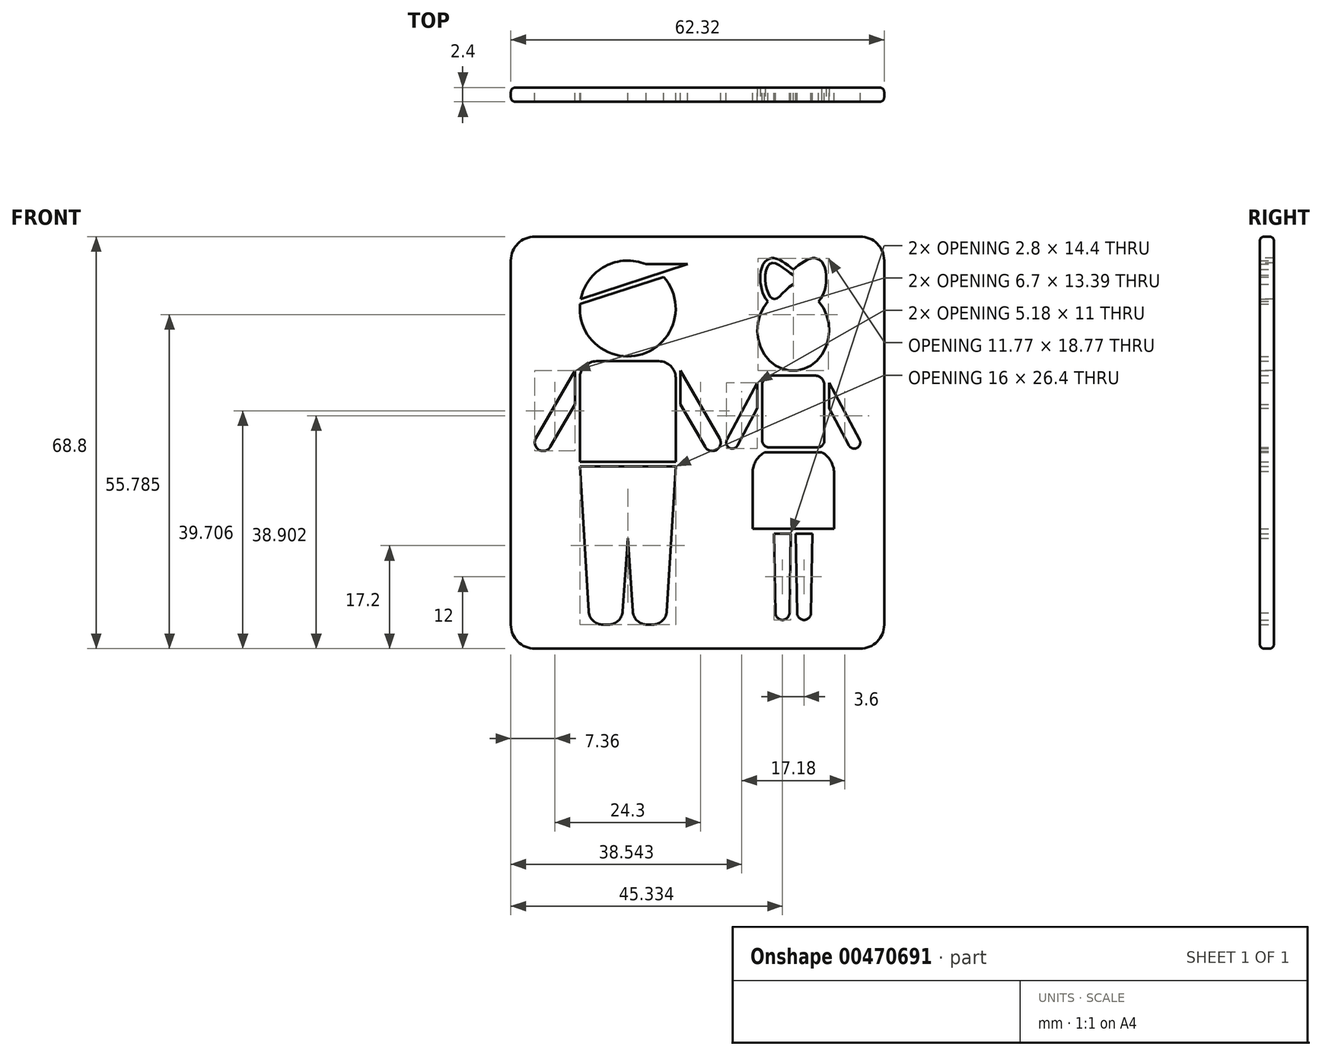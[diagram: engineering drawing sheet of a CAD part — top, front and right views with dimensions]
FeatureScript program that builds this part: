
annotation { "Feature Type Name" : "Feature", "Feature Type Description" : "" }
export const myFeature = defineFeature(function(context is Context, id is Id, definition is map)
    precondition{}
    {
        {
            var Q0;
            Q0=qCreatedBy(makeId("Front.planeOp"),FACE);
            var sketch = newSketch(context, id + "F0", { "sketchPlane" : qUnion([Q0])});
            skLineSegment(sketch, "E0", {"start": v(-25, 66) * mm, "end": v(-25, 0) * mm, "construction": true});
            skArc(sketch, "E1", {"start": v(-21.19, 75.25) * mm, "mid": v(-29.7, 74.83) * mm, "end": v(-34.8, 68) * mm});
            skLineSegment(sketch, "E2.bottom", {"start": v(-31.5, 55) * mm, "end": v(-18.5, 55) * mm});
            skLineSegment(sketch, "E2.top", {"start": v(-35, 34) * mm, "end": v(-15, 34) * mm});
            skLineSegment(sketch, "E2.left", {"start": v(-35, 51.5) * mm, "end": v(-35, 34) * mm});
            skLineSegment(sketch, "E2.right", {"start": v(-15, 51.5) * mm, "end": v(-15, 34) * mm});
            skPoint(sketch, "E2.middle", {"position": v(-25, 44.5) * mm});
            skPoint(sketch, "E3.visualSharp", {"position": v(-15, 55) * mm});
            skArc(sketch, "E3.filletArc", {"start": v(-15, 51.5) * mm, "mid": v(-16.03, 53.97) * mm, "end": v(-18.5, 55) * mm});
            skPoint(sketch, "E4.visualSharp", {"position": v(-35, 55) * mm});
            skArc(sketch, "E4.filletArc", {"start": v(-31.5, 55) * mm, "mid": v(-33.97, 53.97) * mm, "end": v(-35, 51.5) * mm});
            skLineSegment(sketch, "E5", {"start": v(-35, 66) * mm, "end": v(-15, 66) * mm, "construction": true});
            skLineSegment(sketch, "E6", {"start": v(-34.8, 68) * mm, "end": v(-12.5, 75.25) * mm});
            skLineSegment(sketch, "E7", {"start": v(-12.5, 75.25) * mm, "end": v(-21.19, 75.25) * mm});
            skLineSegment(sketch, "E8", {"start": v(-34.96, 66.9) * mm, "end": v(-17.47, 72.58) * mm});
            skLineSegment(sketch, "E9", {"start": v(-35, 33) * mm, "end": v(-15, 33) * mm});
            skLineSegment(sketch, "E10", {"start": v(-35, 33) * mm, "end": v(-33.15, 2.82) * mm});
            skLineSegment(sketch, "E11", {"start": v(-30.16, 0) * mm, "end": v(-29.06, 0) * mm});
            skLineSegment(sketch, "E12", {"start": v(-26.06, 2.8) * mm, "end": v(-25, 18) * mm});
            skPoint(sketch, "E13.visualSharp", {"position": v(-26.26, 0) * mm});
            skArc(sketch, "E13.filletArc", {"start": v(-29.06, 0) * mm, "mid": v(-27.01, 0.8) * mm, "end": v(-26.06, 2.8) * mm});
            skPoint(sketch, "E14.visualSharp", {"position": v(-32.98, 0) * mm});
            skArc(sketch, "E14.filletArc", {"start": v(-33.15, 2.82) * mm, "mid": v(-32.22, 0.81) * mm, "end": v(-30.16, 0) * mm});
            skLineSegment(sketch, "E15.MirrorCS", {"start": v(-15, 33) * mm, "end": v(-16.85, 2.82) * mm});
            skArc(sketch, "E16.MirrorCS", {"start": v(-16.85, 2.82) * mm, "mid": v(-17.78, 0.81) * mm, "end": v(-19.84, 0) * mm});
            skLineSegment(sketch, "E17.MirrorCS", {"start": v(-19.84, 0) * mm, "end": v(-20.94, 0) * mm});
            skArc(sketch, "E18.MirrorCS", {"start": v(-20.94, 0) * mm, "mid": v(-22.99, 0.8) * mm, "end": v(-23.94, 2.8) * mm});
            skLineSegment(sketch, "E19.MirrorCS", {"start": v(-23.94, 2.8) * mm, "end": v(-25, 18) * mm});
            skLineSegment(sketch, "E20", {"start": v(-36, 53) * mm, "end": v(-44.16, 38.88) * mm});
            skLineSegment(sketch, "E21", {"start": v(-41.12, 37.13) * mm, "end": v(-36, 46) * mm});
            skLineSegment(sketch, "E22", {"start": v(-36, 46) * mm, "end": v(-36, 53) * mm});
            skArc(sketch, "E23", {"start": v(-44.16, 38.88) * mm, "mid": v(-43.51, 36.48) * mm, "end": v(-41.12, 37.13) * mm});
            skLineSegment(sketch, "E24.MirrorCS", {"start": v(-14, 53) * mm, "end": v(-5.84, 38.88) * mm});
            skLineSegment(sketch, "E25.MirrorCS", {"start": v(-8.88, 37.13) * mm, "end": v(-14, 46) * mm});
            skLineSegment(sketch, "E26.MirrorCS", {"start": v(-14, 46) * mm, "end": v(-14, 53) * mm});
            skArc(sketch, "E27.MirrorCS", {"start": v(-5.84, 38.88) * mm, "mid": v(-6.49, 36.48) * mm, "end": v(-8.88, 37.13) * mm});
            skArc(sketch, "E28.trimOffspring", {"start": v(-34.96, 66.9) * mm, "mid": v(-21.9, 56.49) * mm, "end": v(-17.47, 72.58) * mm});
            skLineSegment(sketch, "E29", {"start": v(9.53, 1) * mm, "end": v(9.53, 61.5) * mm, "construction": true});
            skLineSegment(sketch, "E30.bottom", {"start": v(5.53, 19) * mm, "end": v(9.03, 19) * mm});
            skLineSegment(sketch, "E30.top", {"start": v(5.82, 2.46) * mm, "end": v(8.74, 2.46) * mm, "construction": true});
            skLineSegment(sketch, "E30.left", {"start": v(5.53, 19) * mm, "end": v(5.82, 2.46) * mm});
            skLineSegment(sketch, "E30.right", {"start": v(9.03, 19) * mm, "end": v(8.74, 2.46) * mm});
            skArc(sketch, "E31", {"start": v(8.74, 2.46) * mm, "mid": v(7.28, 1) * mm, "end": v(5.82, 2.46) * mm});
            skLineSegment(sketch, "E32", {"start": v(5.17, 1) * mm, "end": v(7.83, 1) * mm, "construction": true});
            skLineSegment(sketch, "E33", {"start": v(9.53, 20) * mm, "end": v(1.03, 20) * mm});
            skLineSegment(sketch, "E34", {"start": v(1.03, 20) * mm, "end": v(1.03, 32) * mm});
            skLineSegment(sketch, "E35", {"start": v(9.53, 36) * mm, "end": v(3.53, 36) * mm});
            skArc(sketch, "E36", {"start": v(3.53, 36) * mm, "mid": v(1.8, 34.3) * mm, "end": v(1.03, 32) * mm});
            skLineSegment(sketch, "E37.MirrorCS", {"start": v(13.24, 2.46) * mm, "end": v(10.32, 2.46) * mm, "construction": true});
            skArc(sketch, "E38.MirrorCS", {"start": v(10.32, 2.46) * mm, "mid": v(11.78, 1) * mm, "end": v(13.24, 2.46) * mm});
            skLineSegment(sketch, "E39.MirrorCS", {"start": v(10.03, 19) * mm, "end": v(10.32, 2.46) * mm});
            skLineSegment(sketch, "E40.MirrorCS", {"start": v(13.53, 19) * mm, "end": v(10.03, 19) * mm});
            skLineSegment(sketch, "E41.MirrorCS", {"start": v(13.53, 19) * mm, "end": v(13.24, 2.46) * mm});
            skLineSegment(sketch, "E42.MirrorCS", {"start": v(9.53, 36) * mm, "end": v(15.53, 36) * mm});
            skArc(sketch, "E43.MirrorCS", {"start": v(15.53, 36) * mm, "mid": v(17.26, 34.3) * mm, "end": v(18.03, 32) * mm});
            skLineSegment(sketch, "E44.MirrorCS", {"start": v(18.03, 20) * mm, "end": v(18.03, 32) * mm});
            skLineSegment(sketch, "E45.MirrorCS", {"start": v(9.53, 20) * mm, "end": v(18.03, 20) * mm});
            skLineSegment(sketch, "E46", {"start": v(9.53, 37) * mm, "end": v(4.53, 37) * mm});
            skLineSegment(sketch, "E47", {"start": v(3.03, 38.5) * mm, "end": v(3.03, 50) * mm});
            skLineSegment(sketch, "E48", {"start": v(5.03, 52) * mm, "end": v(9.53, 52) * mm});
            skPoint(sketch, "E49.visualSharp", {"position": v(3.03, 37) * mm});
            skArc(sketch, "E49.filletArc", {"start": v(3.03, 38.5) * mm, "mid": v(3.47, 37.44) * mm, "end": v(4.53, 37) * mm});
            skPoint(sketch, "E50.visualSharp", {"position": v(3.03, 52) * mm});
            skArc(sketch, "E50.filletArc", {"start": v(5.03, 52) * mm, "mid": v(3.62, 51.41) * mm, "end": v(3.03, 50) * mm});
            skLineSegment(sketch, "E51.MirrorCS", {"start": v(14.03, 52) * mm, "end": v(9.53, 52) * mm});
            skArc(sketch, "E52.MirrorCS", {"start": v(14.03, 52) * mm, "mid": v(15.44, 51.41) * mm, "end": v(16.03, 50) * mm});
            skLineSegment(sketch, "E53.MirrorCS", {"start": v(16.03, 38.5) * mm, "end": v(16.03, 50) * mm});
            skArc(sketch, "E54.MirrorCS", {"start": v(16.03, 38.5) * mm, "mid": v(15.6, 37.44) * mm, "end": v(14.53, 37) * mm});
            skLineSegment(sketch, "E55.MirrorCS", {"start": v(9.53, 37) * mm, "end": v(14.53, 37) * mm});
            skLineSegment(sketch, "E56", {"start": v(2.03, 50.5) * mm, "end": v(2.03, 45.17) * mm});
            skLineSegment(sketch, "E57", {"start": v(2.03, 45.17) * mm, "end": v(-2.1, 37.41) * mm});
            skLineSegment(sketch, "E58", {"start": v(-2.1, 37.41) * mm, "end": v(-4.3, 38.59) * mm, "construction": true});
            skLineSegment(sketch, "E59", {"start": v(-4.3, 38.59) * mm, "end": v(2.03, 50.5) * mm});
            skArc(sketch, "E60", {"start": v(-2.1, 37.41) * mm, "mid": v(-3.79, 36.9) * mm, "end": v(-4.3, 38.59) * mm});
            skLineSegment(sketch, "E61.MirrorCS", {"start": v(17.03, 50.5) * mm, "end": v(17.03, 45.17) * mm});
            skLineSegment(sketch, "E62.MirrorCS", {"start": v(23.36, 38.59) * mm, "end": v(17.03, 50.5) * mm});
            skLineSegment(sketch, "E63.MirrorCS", {"start": v(17.03, 45.17) * mm, "end": v(21.16, 37.41) * mm});
            skArc(sketch, "E64.MirrorCS", {"start": v(21.16, 37.41) * mm, "mid": v(22.85, 36.9) * mm, "end": v(23.36, 38.59) * mm});
            skEllipticalArc(sketch, "E65", {});
            skPoint(sketch, "E66.4.internal.snap0", {"position": v(9.53, 70) * mm});
            skFitSpline(sketch, "E66", {"points": [v(9.53, 71.09) * mm, v(5.61, 67.97) * mm, v(3.73, 71.18) * mm, v(5.07, 75.5) * mm, v(9.53, 72.94) * mm], "startDerivative": vector(-20.3, -12.18) * mm, "endDerivative": vector(11.91, -6.98) * mm});
            skFitSpline(sketch, "E67.MirrorCS", {"points": [v(9.53, 71.09) * mm, v(13.45, 67.97) * mm, v(15.33, 71.18) * mm, v(13.98, 75.5) * mm, v(9.53, 72.94) * mm], "startDerivative": vector(20.3, -12.18) * mm, "endDerivative": vector(-11.91, -6.98) * mm});
            skFitSpline(sketch, "E68.0", {"points": [v(10.04, 70.23) * mm, v(9.7, 70.02) * mm, v(9.2, 69.62) * mm, v(8.55, 69) * mm, v(8.08, 68.52) * mm, v(7.62, 68.05) * mm, v(7.15, 67.62) * mm, v(6.72, 67.3) * mm, v(6.3, 67.1) * mm, v(6, 67) * mm, v(5.73, 66.97) * mm, v(5.44, 66.96) * mm, v(5.1, 67.02) * mm, v(4.74, 67.17) * mm, v(4.33, 67.43) * mm, v(3.92, 67.85) * mm, v(3.54, 68.43) * mm, v(3.23, 69.08) * mm, v(2.99, 69.8) * mm, v(2.8, 70.58) * mm, v(2.7, 71.4) * mm, v(2.65, 72.22) * mm, v(2.68, 73.04) * mm, v(2.79, 73.84) * mm, v(2.98, 74.6) * mm, v(3.28, 75.3) * mm, v(3.66, 75.82) * mm, v(4.08, 76.17) * mm, v(4.46, 76.38) * mm, v(4.83, 76.48) * mm, v(5.12, 76.51) * mm, v(5.4, 76.51) * mm, v(5.75, 76.47) * mm, v(6.25, 76.33) * mm, v(6.82, 76.07) * mm, v(7.48, 75.68) * mm, v(8.11, 75.23) * mm, v(8.7, 74.78) * mm, v(9.25, 74.36) * mm, v(9.72, 74) * mm, v(9.95, 73.85) * mm, v(10.04, 73.8) * mm]});
            skFitSpline(sketch, "E69.0", {"points": [v(9.02, 70.23) * mm, v(9.36, 70.02) * mm, v(9.87, 69.62) * mm, v(10.5, 69) * mm, v(10.98, 68.52) * mm, v(11.44, 68.05) * mm, v(11.9, 67.62) * mm, v(12.34, 67.3) * mm, v(12.76, 67.1) * mm, v(13.06, 67) * mm, v(13.33, 66.97) * mm, v(13.61, 66.96) * mm, v(13.95, 67.02) * mm, v(14.32, 67.17) * mm, v(14.73, 67.43) * mm, v(15.14, 67.85) * mm, v(15.52, 68.43) * mm, v(15.83, 69.08) * mm, v(16.07, 69.8) * mm, v(16.25, 70.58) * mm, v(16.37, 71.4) * mm, v(16.4, 72.22) * mm, v(16.38, 73.04) * mm, v(16.27, 73.84) * mm, v(16.08, 74.6) * mm, v(15.78, 75.3) * mm, v(15.4, 75.82) * mm, v(14.98, 76.17) * mm, v(14.6, 76.38) * mm, v(14.23, 76.48) * mm, v(13.94, 76.51) * mm, v(13.65, 76.51) * mm, v(13.31, 76.47) * mm, v(12.81, 76.33) * mm, v(12.23, 76.07) * mm, v(11.58, 75.68) * mm, v(10.95, 75.23) * mm, v(10.35, 74.78) * mm, v(9.8, 74.36) * mm, v(9.34, 74) * mm, v(9.1, 73.85) * mm, v(9.02, 73.8) * mm]});
            const initialGuessF0  = {"E65": [0.009529412724077696, 0.0615, 0, -1, 0.0085, 0.0075, 3.9233208754425206, 2.359864431737064]};
            skSetInitialGuess(sketch, initialGuessF0);
            skSolve(sketch);
        }
        {
            var Q0;
            Q0=qCreatedBy(makeId("Front.planeOp"),FACE);
            var sketch = newSketch(context, id + "F1", { "sketchPlane" : qUnion([Q0])});
            skLineSegment(sketch, "E70.bottom", {"start": v(-49.39, 81) * mm, "end": v(28.51, 81) * mm});
            skLineSegment(sketch, "E70.top", {"start": v(-49.39, -5) * mm, "end": v(28.51, -5) * mm});
            skLineSegment(sketch, "E70.left", {"start": v(-49.39, 81) * mm, "end": v(-49.39, -5) * mm});
            skLineSegment(sketch, "E70.right", {"start": v(28.51, 81) * mm, "end": v(28.51, -5) * mm});
            skArc(sketch, "E71.0", {"start": v(-44.16, 38.88) * mm, "mid": v(-43.51, 36.48) * mm, "end": v(-41.12, 37.13) * mm, "construction": true});
            skArc(sketch, "E72.0", {"start": v(-21.19, 75.25) * mm, "mid": v(-29.7, 74.83) * mm, "end": v(-34.8, 68) * mm, "construction": true});
            skArc(sketch, "E73.0", {"start": v(21.16, 37.41) * mm, "mid": v(22.85, 36.9) * mm, "end": v(23.36, 38.59) * mm, "construction": true});
            skSolve(sketch);
        }
        {
            var Q0;
            Q0 = qSketchRegion(id + "F1", true);
            extrude(context, id + "F2", {"entities" : qUnion([Q0]), "depth" : 3 * mm});
        }
        {
            var Q0;
            Q0 = qSketchRegion(id + "F0", true);
            extrude(context, id + "F3", {"entities" : qUnion([Q0]), "operationType" : NewBodyOperationType.REMOVE, "endBound" : BoundingType.THROUGH_ALL, "depth" : 25 * mm});
        }
        {
            var Q0;
            Q0=makeQuery(id+"F2.opExtrude","SWEPT_EDGE",EDGE,{"disambiguationData":[OSD([sQuery(id+"F1.wireOp",EDGE,"E70.bottom"),sQuery(id+"F1.wireOp",EDGE,"E70.right")])]});
            var Q1;
            Q1=makeQuery(id+"F2.opExtrude","SWEPT_EDGE",EDGE,{"disambiguationData":[OSD([sQuery(id+"F1.wireOp",EDGE,"E70.top"),sQuery(id+"F1.wireOp",EDGE,"E70.right")])]});
            var Q2;
            Q2=makeQuery(id+"F2.opExtrude","SWEPT_EDGE",EDGE,{"disambiguationData":[OSD([sQuery(id+"F1.wireOp",EDGE,"E70.top"),sQuery(id+"F1.wireOp",EDGE,"E70.left")])]});
            var Q3;
            Q3=makeQuery(id+"F2.opExtrude","SWEPT_EDGE",EDGE,{"disambiguationData":[OSD([sQuery(id+"F1.wireOp",EDGE,"E70.bottom"),sQuery(id+"F1.wireOp",EDGE,"E70.left")])]});
            fillet(context, id + "F4", {"entities" : qUnion([Q0, Q1, Q2, Q3]), "radius" : 5 * mm, "tangentPropagation" : true, "allowEdgeOverflow" : false});
        }
        {
            var Q0;
            Q0=makeQuery(id+"F2.opExtrude","CAP_EDGE",EDGE,{"disambiguationData":[OSD([sQuery(id+"F1.wireOp",EDGE,"E70.bottom")])],"isStart":false});
            var Q1;
            Q1=makeQuery(id+"F2.opExtrude","CAP_EDGE",EDGE,{"disambiguationData":[OSD([sQuery(id+"F1.wireOp",EDGE,"E70.bottom")])],"isStart":true});
            fillet(context, id + "F5", {"entities" : qUnion([Q0, Q1]), "radius" : 1 * mm, "tangentPropagation" : true, "allowEdgeOverflow" : false});
        }
        {
            var Q0;
            Q0=makeQuery(id+"F2.opExtrude","SWEPT_BODY",BODY,{"disambiguationData":[OSD([sQuery(id+"F1.wireOp",EDGE,"E70.bottom"),sQuery(id+"F1.wireOp",EDGE,"E70.top"),sQuery(id+"F1.wireOp",EDGE,"E70.left"),sQuery(id+"F1.wireOp",EDGE,"E70.right")])]});
            var Q1;
            Q1=qCreatedBy(makeId("Origin.pointOp"),VERTEX);
            transform(context, id + "F6", {"entities" : qUnion([Q0]), "transformType" : TransformType.SCALE_UNIFORMLY, "scale" : 0.8, "scalePoint" : qUnion([Q1]), "makeCopy" : false});
        }
    });
